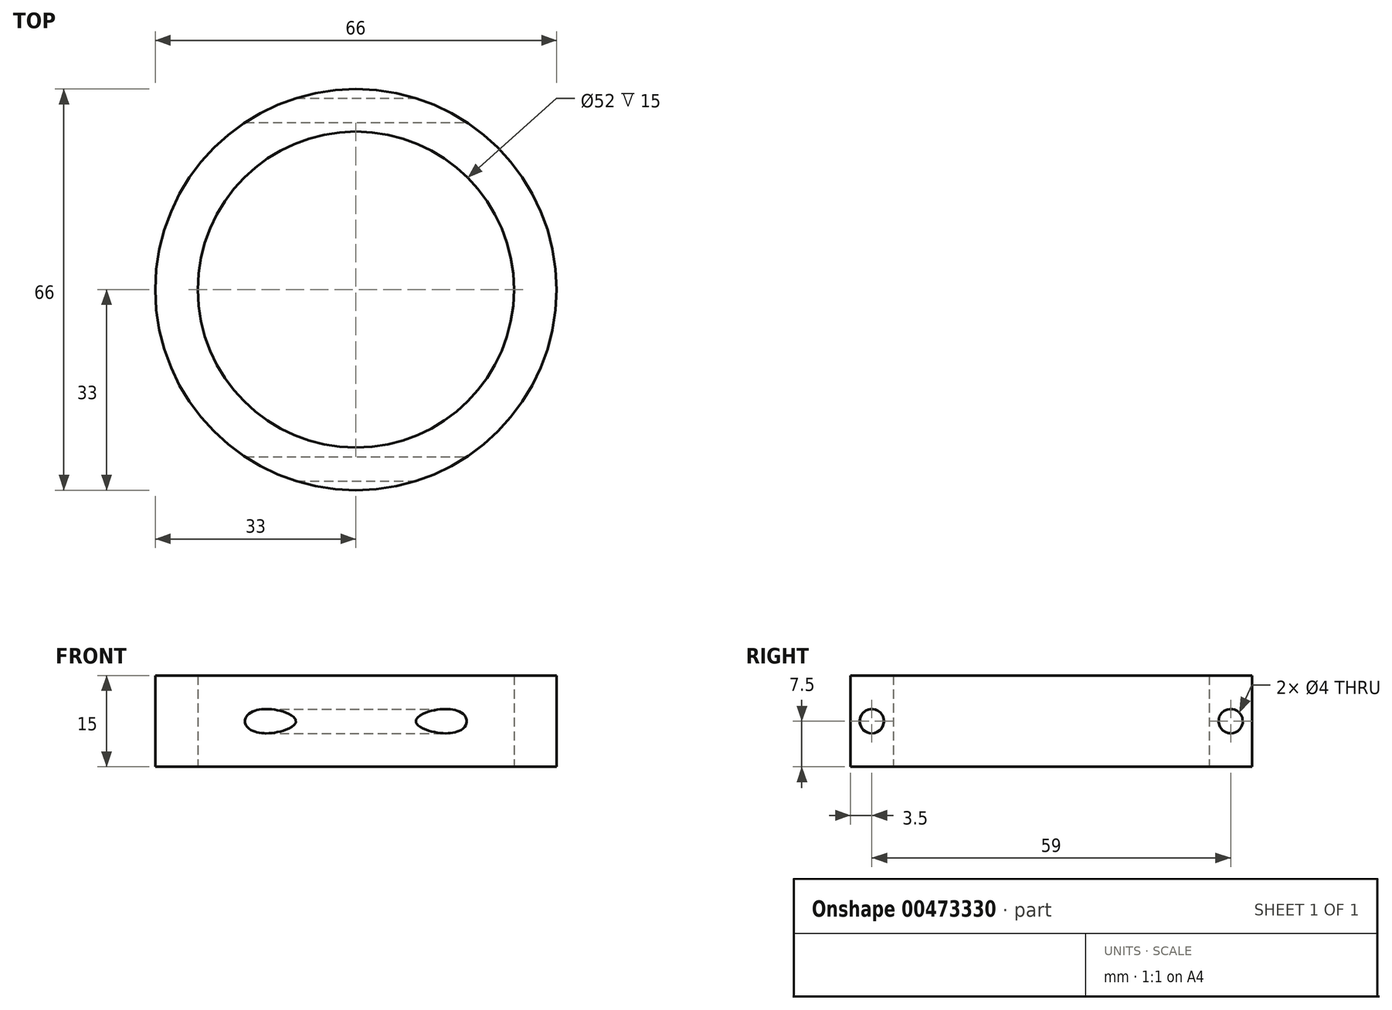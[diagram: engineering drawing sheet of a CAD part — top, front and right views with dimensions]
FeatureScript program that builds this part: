
annotation { "Feature Type Name" : "Feature", "Feature Type Description" : "" }
export const myFeature = defineFeature(function(context is Context, id is Id, definition is map)
    precondition{}
    {
        {
            var Q0;
            Q0=qCreatedBy(makeId("Top.planeOp"),FACE);
            var sketch = newSketch(context, id + "F0", { "sketchPlane" : qUnion([Q0])});
            skCircle(sketch, "E0", {"center": v(0, 0) * mm, "radius": 26 * mm});
            skCircle(sketch, "E1", {"center": v(0, 0) * mm, "radius": 33 * mm});
            skSolve(sketch);
        }
        {
            var Q0;
            Q0 = qSketchRegion(id + "F0", true);
            extrude(context, id + "F1", {"entities" : qUnion([Q0]), "depth" : 15 * mm});
        }
        {
            var Q0;
            Q0=qCreatedBy(makeId("Right.planeOp"),FACE);
            var sketch = newSketch(context, id + "F2", { "sketchPlane" : qUnion([Q0])});
            skLineSegment(sketch, "E2", {"start": v(0, 15) * mm, "end": v(0, 0) * mm, "construction": true});
            skLineSegment(sketch, "E3", {"start": v(33, 15.94) * mm, "end": v(33, -3.8) * mm, "construction": true});
            skLineSegment(sketch, "E4", {"start": v(26, 19.59) * mm, "end": v(26, -5.9) * mm, "construction": true});
            skCircle(sketch, "E5", {"center": v(29.5, 7.5) * mm, "radius": 2 * mm});
            skCircle(sketch, "E6", {"center": v(-29.5, 7.5) * mm, "radius": 2 * mm});
            skSolve(sketch);
        }
        {
            var Q0;
            Q0 = qSketchRegion(id + "F2", true);
            extrude(context, id + "F3", {"entities" : qUnion([Q0]), "operationType" : NewBodyOperationType.REMOVE, "endBound" : BoundingType.THROUGH_ALL, "oppositeDirection" : true, "depth" : 25 * mm, "hasSecondDirection" : true, "secondDirectionBound" : SecondDirectionBoundingType.THROUGH_ALL, "secondDirectionOppositeDirection" : false, "secondDirectionDepth" : 25 * mm});
        }
    });
